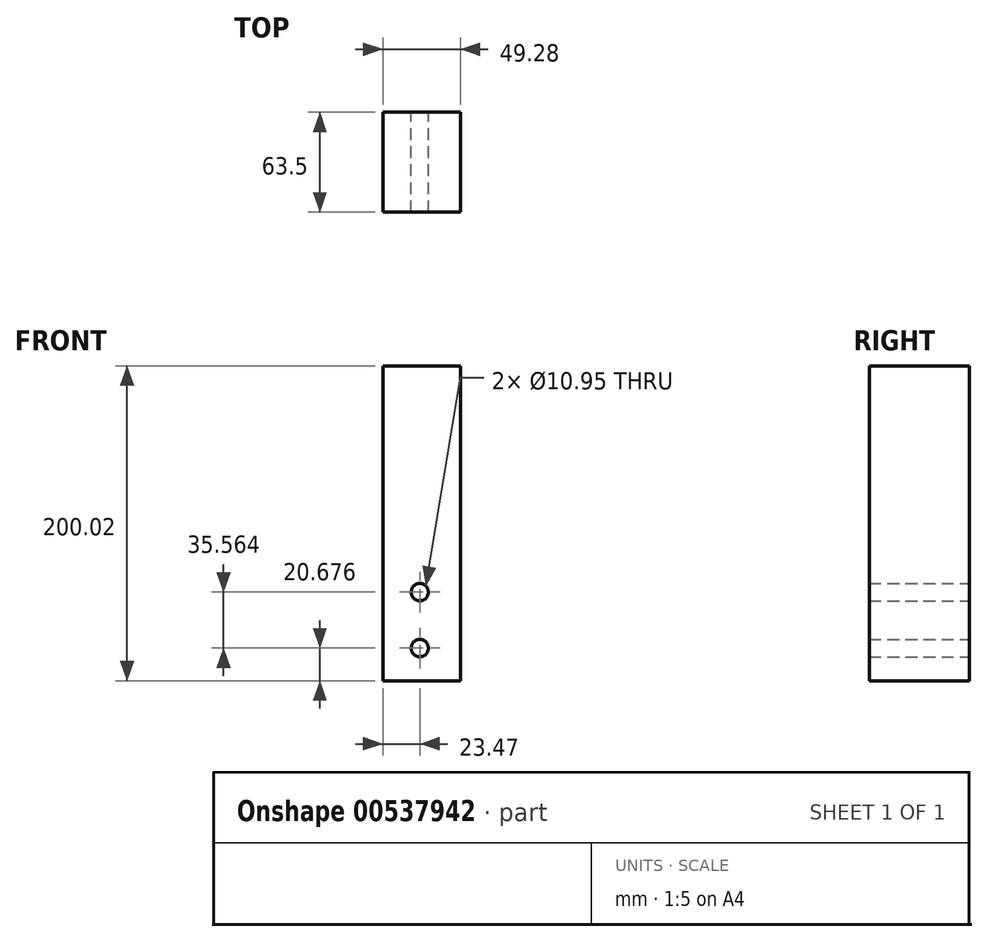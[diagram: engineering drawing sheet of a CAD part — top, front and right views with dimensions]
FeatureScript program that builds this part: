
annotation { "Feature Type Name" : "Feature", "Feature Type Description" : "" }
export const myFeature = defineFeature(function(context is Context, id is Id, definition is map)
    precondition{}
    {
        {
            var Q0;
            Q0=qCreatedBy(makeId("Front.planeOp"),FACE);
            var sketch = newSketch(context, id + "F0", { "sketchPlane" : qUnion([Q0])});
            skLineSegment(sketch, "E0.bottom", {"start": v(-23.47, 143.78) * mm, "end": v(25.8, 143.78) * mm});
            skLineSegment(sketch, "E0.top", {"start": v(-23.47, -56.24) * mm, "end": v(25.8, -56.24) * mm});
            skLineSegment(sketch, "E0.left", {"start": v(-23.47, 143.78) * mm, "end": v(-23.47, -56.24) * mm});
            skLineSegment(sketch, "E0.right", {"start": v(25.8, 143.78) * mm, "end": v(25.8, -56.24) * mm});
            skCircle(sketch, "E1", {"center": v(0, 0) * mm, "radius": 5.47 * mm});
            skCircle(sketch, "E2", {"center": v(0, -35.56) * mm, "radius": 5.47 * mm});
            skSolve(sketch);
        }
        {
            var Q0;
            Q0=makeQuery(id+"F0.imprint","IMPRINT",FACE,{"disambiguationData":[TD([[makeQuery(id+"F0.imprint","IMPRINT",EDGE,{"derivedFrom":sQuery(id+"F0.wireOp",EDGE,"E0.bottom")}),-1.0]])]});
            extrude(context, id + "F1", {"entities" : qUnion([Q0]), "depth" : 63.5 * mm, "offsetDistance" : 25.4 * mm});
        }
    });
